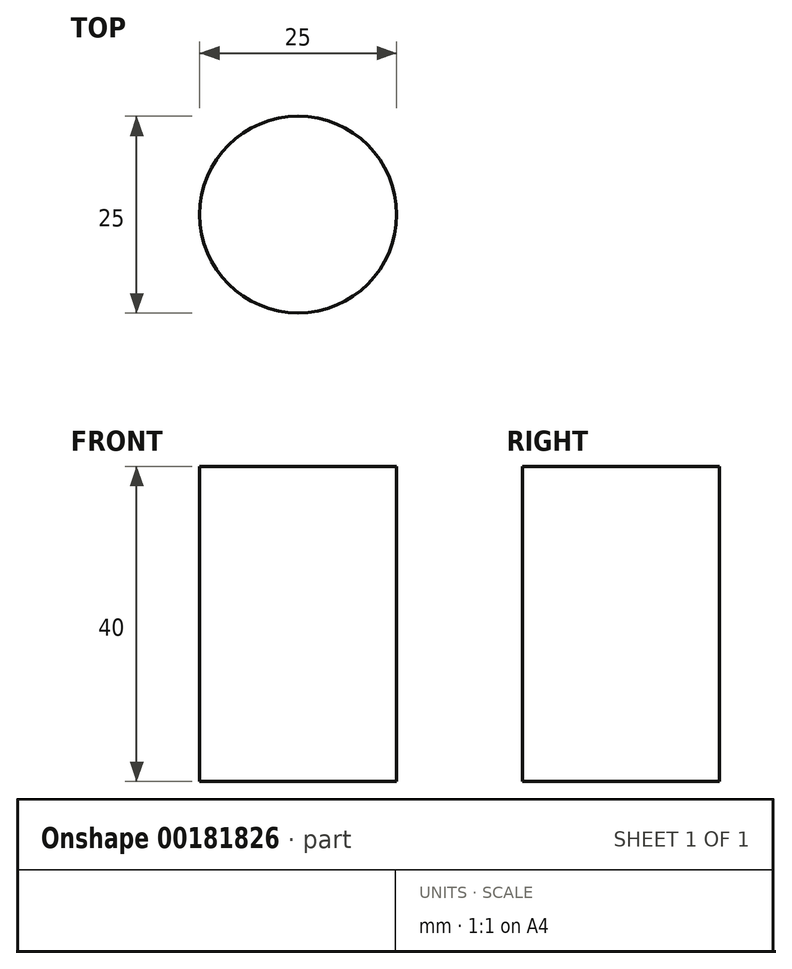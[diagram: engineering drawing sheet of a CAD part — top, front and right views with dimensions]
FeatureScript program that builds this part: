
annotation { "Feature Type Name" : "Feature", "Feature Type Description" : "" }
export const myFeature = defineFeature(function(context is Context, id is Id, definition is map)
    precondition{}
    {
        {
            var Q0;
            Q0=qCreatedBy(makeId("Front.planeOp"),FACE);
            var sketch = newSketch(context, id + "F0", { "sketchPlane" : qUnion([Q0])});
            skLineSegment(sketch, "E0.bottom", {"start": v(0, 0) * mm, "end": v(-12.5, 0) * mm});
            skLineSegment(sketch, "E0.top", {"start": v(0, 40) * mm, "end": v(-12.5, 40) * mm});
            skLineSegment(sketch, "E0.left", {"start": v(0, 0) * mm, "end": v(0, 40) * mm});
            skLineSegment(sketch, "E0.right", {"start": v(-12.5, 0) * mm, "end": v(-12.5, 40) * mm});
            skSolve(sketch);
        }
        {
            var Q0;
            Q0 = qSketchRegion(id + "F0", true);
            var Q1;
            Q1=sQuery(id+"F0.wireOp",EDGE,"E0.left");
            revolve(context, id + "F1", {"entities" : qUnion([Q0]), "axis" : qUnion([Q1]), "revolveType" : RevolveType.FULL});
        }
    });
